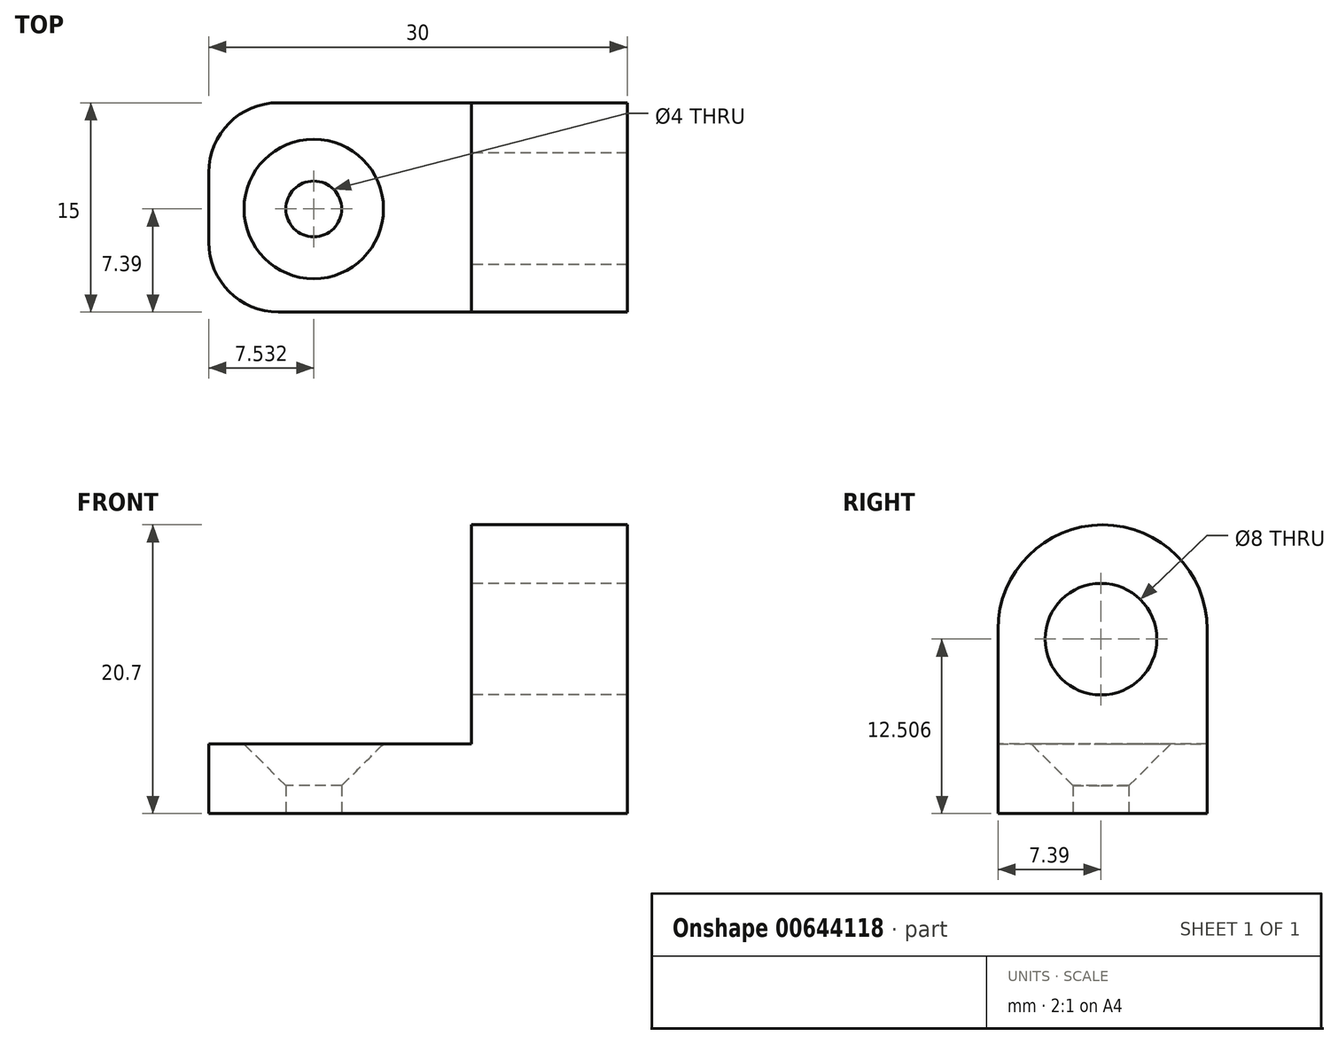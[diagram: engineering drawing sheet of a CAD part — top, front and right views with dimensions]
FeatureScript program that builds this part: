
annotation { "Feature Type Name" : "Feature", "Feature Type Description" : "" }
export const myFeature = defineFeature(function(context is Context, id is Id, definition is map)
    precondition{}
    {
        {
            var Q0;
            Q0=qCreatedBy(makeId("Top.planeOp"),FACE);
            var sketch = newSketch(context, id + "F0", { "sketchPlane" : qUnion([Q0])});
            skLineSegment(sketch, "E0.bottom", {"start": v(0.05, 7.61) * mm, "end": v(30.05, 7.61) * mm});
            skLineSegment(sketch, "E0.top", {"start": v(0.05, -7.39) * mm, "end": v(30.05, -7.39) * mm});
            skLineSegment(sketch, "E0.left", {"start": v(0.05, 7.61) * mm, "end": v(0.05, -7.39) * mm});
            skLineSegment(sketch, "E0.right", {"start": v(30.05, 7.61) * mm, "end": v(30.05, -7.39) * mm});
            skCircle(sketch, "E1", {"center": v(7.58, 0) * mm, "radius": 2 * mm});
            skLineSegment(sketch, "E2", {"start": v(18.9, 7.61) * mm, "end": v(18.9, -7.39) * mm});
            skSolve(sketch);
        }
        {
            var Q0;
            {var subQ0=sQuery(id+"F0.wireOp",EDGE,"E0.left");Q0=makeQuery(id+"F0.imprint","IMPRINT",FACE,{"disambiguationData":[TD([[makeQuery(id+"F0.imprint","IMPRINT",EDGE,{"derivedFrom":subQ0}),1.0]])]});}
            var Q1;
            {var subQ0=sQuery(id+"F0.wireOp",EDGE,"E0.right");Q1=makeQuery(id+"F0.imprint","IMPRINT",FACE,{"disambiguationData":[TD([[makeQuery(id+"F0.imprint","IMPRINT",EDGE,{"derivedFrom":subQ0}),-1.0]])]});}
            extrude(context, id + "F1", {"entities" : qUnion([Q0, Q1]), "depth" : 5 * mm, "offsetDistance" : 25 * mm});
        }
        {
            var Q0;
            Q0=makeQuery(id+"F1.opExtrude","CAP_EDGE",EDGE,{"disambiguationData":[OSD([sQuery(id+"F0.wireOp",EDGE,"E1")])],"isStart":false});
            chamfer(context, id + "F2", {"entities" : qUnion([Q0]), "width" : 3 * mm, "tangentPropagation" : true});
        }
        {
            var Q0;
            {var subQ0=sQuery(id+"F0.wireOp",EDGE,"E0.right");Q0=makeQuery(id+"F0.imprint","IMPRINT",FACE,{"disambiguationData":[TD([[makeQuery(id+"F0.imprint","IMPRINT",EDGE,{"derivedFrom":subQ0}),-1.0]])]});}
            extrude(context, id + "F3", {"entities" : qUnion([Q0]), "operationType" : NewBodyOperationType.ADD, "depth" : 20.7 * mm, "offsetDistance" : 25 * mm});
        }
        {
            var Q0;
            Q0=qCreatedBy(makeId("Right.planeOp"),FACE);
            var sketch = newSketch(context, id + "F4", { "sketchPlane" : qUnion([Q0])});
            skCircle(sketch, "E3", {"center": v(0, 12.5) * mm, "radius": 4 * mm});
            skSolve(sketch);
        }
        {
            var Q0;
            Q0=makeQuery(id+"F4.imprint","IMPRINT",FACE,{"disambiguationData":[TD([[makeQuery(id+"F4.imprint","IMPRINT",EDGE,{"derivedFrom":sQuery(id+"F4.wireOp",EDGE,"E3")}),1.0]])]});
            extrude(context, id + "F5", {"entities" : qUnion([Q0]), "operationType" : NewBodyOperationType.REMOVE, "depth" : 55.3 * mm, "offsetDistance" : 25 * mm});
        }
        {
            var Q0;
            Q0=makeQuery(id+"F3.opExtrude","CAP_EDGE",EDGE,{"disambiguationData":[OSD([sQuery(id+"F0.wireOp",EDGE,"E0.top")])],"isStart":false});
            var Q1;
            Q1=makeQuery(id+"F3.opExtrude","CAP_EDGE",EDGE,{"disambiguationData":[OSD([sQuery(id+"F0.wireOp",EDGE,"E0.bottom")])],"isStart":false});
            fillet(context, id + "F6", {"entities" : qUnion([Q0, Q1]), "radius" : 7.5 * mm, "tangentPropagation" : true, "allowEdgeOverflow" : false});
        }
        {
            var Q0;
            Q0=makeQuery(id+"F1.opExtrude","SWEPT_EDGE",EDGE,{"disambiguationData":[OSD([sQuery(id+"F0.wireOp",EDGE,"E0.top"),sQuery(id+"F0.wireOp",EDGE,"E0.left")])]});
            var Q1;
            Q1=makeQuery(id+"F1.opExtrude","SWEPT_EDGE",EDGE,{"disambiguationData":[OSD([sQuery(id+"F0.wireOp",EDGE,"E0.bottom"),sQuery(id+"F0.wireOp",EDGE,"E0.left")])]});
            fillet(context, id + "F7", {"entities" : qUnion([Q0, Q1]), "radius" : 5 * mm, "tangentPropagation" : true, "allowEdgeOverflow" : false});
        }
    });
